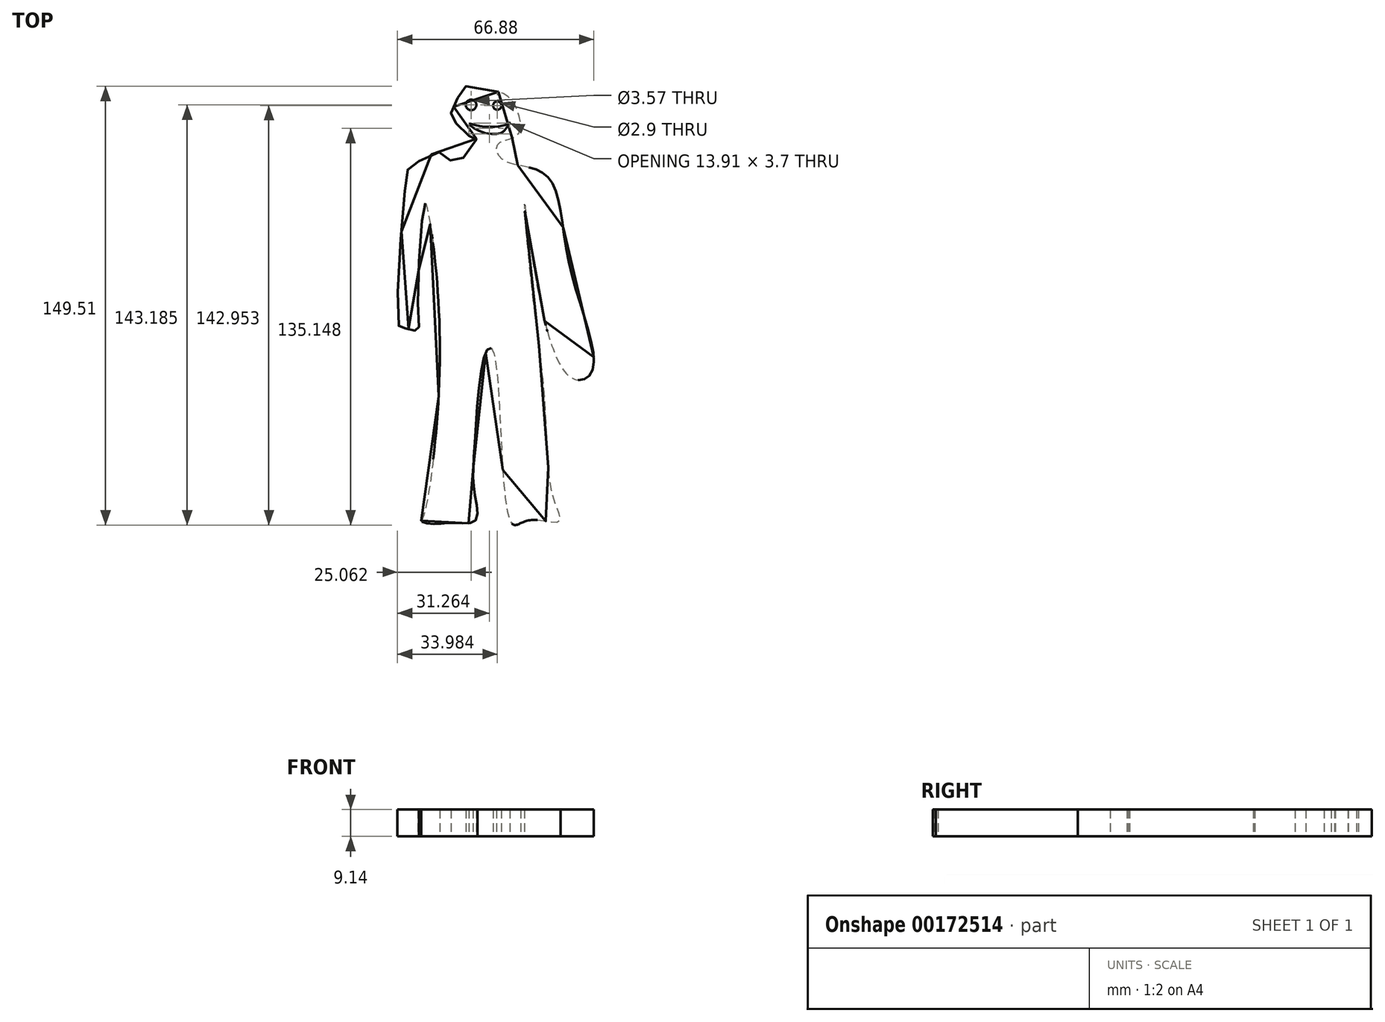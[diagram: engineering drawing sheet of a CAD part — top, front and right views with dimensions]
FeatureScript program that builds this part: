
annotation { "Feature Type Name" : "Feature", "Feature Type Description" : "" }
export const myFeature = defineFeature(function(context is Context, id is Id, definition is map)
    precondition{}
    {
        {
            var Q0;
            Q0=qCreatedBy(makeId("Top.planeOp"),FACE);
            var sketch = newSketch(context, id + "F0", { "sketchPlane" : qUnion([Q0])});
            skFitSpline(sketch, "E0", {"points": [v(-114.38, 67.08) * mm, v(-124.57, 68.65) * mm, v(-126.14, 68.65) * mm, v(-130.44, 60.03) * mm, v(-130.44, 59.25) * mm, v(-124.96, 52.2) * mm, v(-121.83, 51.41) * mm, v(-129.27, 42.8) * mm, v(-133.19, 46.32) * mm, v(-144.16, 41.62) * mm, v(-145.72, 38.49) * mm, v(-148.07, -13.61) * mm, v(-146.5, -13.61) * mm, v(-143.76, -14) * mm, v(-141.8, -14.4) * mm, v(-141.8, -7.74) * mm, v(-139.45, 29.09) * mm, v(-139.06, 28.7) * mm, v(-134.36, -19.88) * mm, v(-140.24, -78.25) * mm, v(-140.63, -79.42) * mm, v(-135.93, -80.2) * mm, v(-129.27, -79.81) * mm, v(-122.22, -79.03) * mm, v(-122.61, -69.24) * mm, v(-122.61, -55.14) * mm, v(-118.3, -21.06) * mm, v(-116.34, -21.06) * mm, v(-110.07, -79.81) * mm, v(-104.2, -79.03) * mm, v(-93.62, -79.42) * mm, v(-95.58, -71.59) * mm, v(-98.32, -41.82) * mm, v(-103.42, 4.4) * mm, v(-105.37, 28.3) * mm, v(-91.66, -28.5) * mm, v(-82.65, -28.5) * mm, v(-90.1, 7.54) * mm, v(-97.54, 38.1) * mm, v(-109.3, 42.4) * mm, v(-114.38, 45.54) * mm, v(-114.38, 49.46) * mm, v(-107.72, 52.59) * mm, v(-108.5, 62) * mm, v(-114.38, 67.08) * mm]});
            skCircle(sketch, "E1", {"center": v(-123.72, 62.6) * mm, "radius": 1.78 * mm});
            skCircle(sketch, "E2", {"center": v(-114.8, 62.36) * mm, "radius": 1.45 * mm});
            skFitSpline(sketch, "E3", {"points": [v(-124.47, 56.16) * mm, v(-119.6, 53.2) * mm, v(-113.12, 53.2) * mm, v(-111.96, 54.43) * mm, v(-110.5, 56.57) * mm, v(-111.67, 56) * mm, v(-114.8, 55.24) * mm, v(-121, 55.47) * mm, v(-124.47, 56.16) * mm]});
            skSolve(sketch);
        }
        {
            var Q0;
            Q0=makeQuery(id+"F0.imprint","IMPRINT",FACE,{"disambiguationData":[TD([[makeQuery(id+"F0.imprint","IMPRINT",EDGE,{"derivedFrom":sQuery(id+"F0.wireOp",EDGE,"E0")}),1.0]])]});
            extrude(context, id + "F1", {"entities" : qUnion([Q0]), "depth" : 9.14 * mm});
        }
    });
